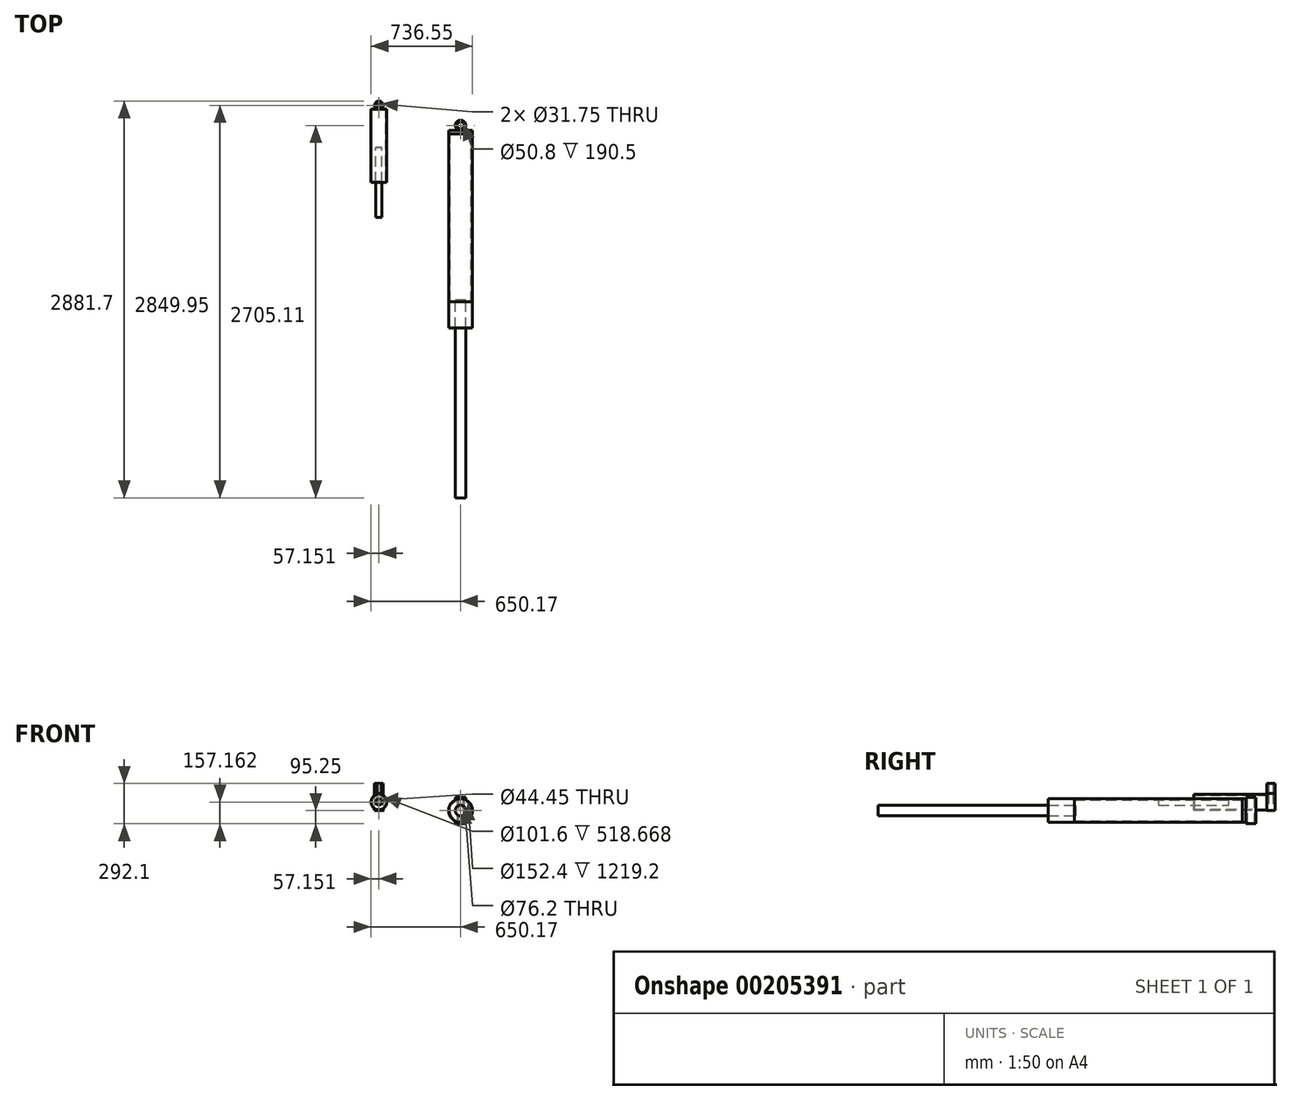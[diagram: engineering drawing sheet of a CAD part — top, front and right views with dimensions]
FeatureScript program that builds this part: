
annotation { "Feature Type Name" : "Feature", "Feature Type Description" : "" }
export const myFeature = defineFeature(function(context is Context, id is Id, definition is map)
    precondition{}
    {
        {
            var Q0;
            Q0=qCreatedBy(makeId("Front.planeOp"),FACE);
            var sketch = newSketch(context, id + "F0", { "sketchPlane" : qUnion([Q0])});
            skCircle(sketch, "E0", {"center": v(0, 0) * mm, "radius": 85.73 * mm});
            skCircle(sketch, "E1.0", {"center": v(0, 0) * mm, "radius": 76.2 * mm});
            skSolve(sketch);
        }
        {
            var Q0;
            Q0=makeQuery(id+"F0.imprint","IMPRINT",FACE,{"disambiguationData":[TD([[makeQuery(id+"F0.imprint","IMPRINT",EDGE,{"derivedFrom":sQuery(id+"F0.wireOp",EDGE,"E0")}),1.0]])]});
            extrude(context, id + "F1", {"entities" : qUnion([Q0]), "depth" : 1219.2 * mm});
        }
        {
            var Q0;
            Q0=makeQuery(id+"F1.opExtrude","CAP_FACE",FACE,{"disambiguationData":[OSD([sQuery(id+"F0.wireOp",EDGE,"E0"),sQuery(id+"F0.wireOp",EDGE,"E1.0")])],"isStart":false});
            var sketch = newSketch(context, id + "F2", { "sketchPlane" : qUnion([Q0])});
            skCircle(sketch, "E2", {"center": v(0, 0) * mm, "radius": 85.59 * mm});
            skCircle(sketch, "E3", {"center": v(0, 0) * mm, "radius": 38.1 * mm});
            skSolve(sketch);
        }
        {
            var Q0;
            Q0=makeQuery(id+"F2.imprint","IMPRINT",FACE,{"disambiguationData":[TD([[makeQuery(id+"F2.imprint","IMPRINT",EDGE,{"derivedFrom":sQuery(id+"F2.wireOp",EDGE,"E2")}),1.0]])]});
            var Q1;
            Q1=makeQuery(id+"F2.imprint","IMPRINT",FACE,{"disambiguationData":[TD([[makeQuery(id+"F2.imprint","IMPRINT",EDGE,{"derivedFrom":sQuery(id+"F2.wireOp",EDGE,"E3")}),-1.0]])]});
            extrude(context, id + "F3", {"entities" : qUnion([Q0, Q1]), "operationType" : NewBodyOperationType.ADD, "depth" : 190.5 * mm});
        }
        {
            var Q0;
            Q0=makeQuery(id+"F1.opExtrude","CAP_FACE",FACE,{"disambiguationData":[OSD([sQuery(id+"F0.wireOp",EDGE,"E0"),sQuery(id+"F0.wireOp",EDGE,"E1.0")])],"isStart":true});
            var sketch = newSketch(context, id + "F4", { "sketchPlane" : qUnion([Q0])});
            skCircle(sketch, "E4", {"center": v(0, 0) * mm, "radius": 86.38 * mm});
            skSolve(sketch);
        }
        {
            var Q0;
            Q0=makeQuery(id+"F4.imprint","IMPRINT",FACE,{"disambiguationData":[TD([[makeQuery(id+"F4.imprint","IMPRINT",EDGE,{"derivedFrom":sQuery(id+"F4.wireOp",EDGE,"E4")}),1.0]])]});
            var Q1;
            Q1=makeQuery(id+"F4.imprint","IMPRINT",FACE,{"disambiguationData":[TD([[makeQuery(id+"F4.imprint","IMPRINT",EDGE,{"derivedFrom":makeQuery(id+"F1.opExtrude","CAP_EDGE",EDGE,{"disambiguationData":[OSD([sQuery(id+"F0.wireOp",EDGE,"E0")])],"isStart":true})}),-1.0]])]});
            var Q2;
            Q2=makeQuery(id+"F4.imprint","IMPRINT",FACE,{"disambiguationData":[TD([[makeQuery(id+"F4.imprint","IMPRINT",EDGE,{"derivedFrom":makeQuery(id+"F1.opExtrude","CAP_EDGE",EDGE,{"disambiguationData":[OSD([sQuery(id+"F0.wireOp",EDGE,"E1.0")])],"isStart":true})}),-1.0]])]});
            extrude(context, id + "F5", {"entities" : qUnion([Q0, Q1, Q2]), "operationType" : NewBodyOperationType.ADD, "depth" : 25.4 * mm});
        }
        {
            var Q0;
            Q0=qCreatedBy(makeId("Top.planeOp"),FACE);
            var sketch = newSketch(context, id + "F6", { "sketchPlane" : qUnion([Q0])});
            skArc(sketch, "E5", {"start": v(15.23, 25.4) * mm, "mid": v(0, 98.42) * mm, "end": v(-15.23, 25.4) * mm});
            skCircle(sketch, "E6.0", {"center": v(0, 60.33) * mm, "radius": 25.4 * mm});
            skLineSegment(sketch, "E7", {"start": v(15.23, 25.4) * mm, "end": v(-15.23, 25.4) * mm});
            skSolve(sketch);
        }
        {
            var Q0;
            Q0=makeQuery(id+"F6.imprint","IMPRINT",FACE,{"disambiguationData":[TD([[makeQuery(id+"F6.imprint","IMPRINT",EDGE,{"derivedFrom":sQuery(id+"F6.wireOp",EDGE,"E5")}),1.0]])]});
            extrude(context, id + "F7", {"entities" : qUnion([Q0]), "depth" : 190.5 * mm, "symmetric" : true});
        }
        {
            var Q0;
            Q0=makeQuery(id+"F3.opExtrude","CAP_FACE",FACE,{"disambiguationData":[OSD([sQuery(id+"F2.wireOp",EDGE,"E2"),sQuery(id+"F2.wireOp",EDGE,"E3")])],"isStart":false});
            var sketch = newSketch(context, id + "F8", { "sketchPlane" : qUnion([Q0])});
            skCircle(sketch, "E8", {"center": v(0, 0) * mm, "radius": 38.1 * mm});
            skSolve(sketch);
        }
        {
            var Q0;
            Q0 = qSketchRegion(id + "F8", true);
            extrude(context, id + "F9", {"entities" : qUnion([Q0]), "depth" : 1235.07 * mm, "hasSecondDirection" : true, "secondDirectionOppositeDirection" : true, "secondDirectionDepth" : 203.2 * mm});
        }
        {
            var Q0;
            Q0=makeQuery(id+"F1.opExtrude","SWEPT_BODY",BODY,{"disambiguationData":[OSD([sQuery(id+"F0.wireOp",EDGE,"E0"),sQuery(id+"F0.wireOp",EDGE,"E1.0")])]});
            transform(context, id + "F10", {"entities" : qUnion([Q0]), "transformType" : TransformType.TRANSLATION_3D, "dx" : -444.5 * mm, "dy" : 0 * mm, "dz" : 0 * mm, "makeCopy" : true});
        }
        {
            var Q0;
            Q0=makeQuery(id+"F7.opExtrude","SWEPT_BODY",BODY,{"disambiguationData":[OSD([sQuery(id+"F6.wireOp",EDGE,"E5"),sQuery(id+"F6.wireOp",EDGE,"E6.0"),sQuery(id+"F6.wireOp",EDGE,"E7")])]});
            transform(context, id + "F11", {"entities" : qUnion([Q0]), "transformType" : TransformType.TRANSLATION_3D, "dx" : -347.98 * mm, "dy" : 0 * mm, "dz" : 0 * mm, "makeCopy" : true});
        }
        {
            var Q0;
            Q0=makeQuery(id+"F9.opExtrude","SWEPT_BODY",BODY,{"disambiguationData":[OSD([sQuery(id+"F8.wireOp",EDGE,"E8")])]});
            transform(context, id + "F12", {"entities" : qUnion([Q0]), "transformType" : TransformType.TRANSLATION_3D, "dx" : -424.18 * mm, "dy" : 0 * mm, "dz" : 0 * mm, "makeCopy" : true});
        }
        {
            var Q0;
            Q0=makeQuery(id+"F12.opPattern","COPY",BODY,{"derivedFrom":makeQuery(id+"F9.opExtrude","SWEPT_BODY",BODY,{"disambiguationData":[OSD([sQuery(id+"F8.wireOp",EDGE,"E8")])]}),"instanceName":"1"});
            deleteBodies(context, id + "F13", {"entities" : qUnion([Q0])});
        }
        {
            var Q0;
            Q0=makeQuery(id+"F10.opPattern","COPY",BODY,{"derivedFrom":makeQuery(id+"F1.opExtrude","SWEPT_BODY",BODY,{"disambiguationData":[OSD([sQuery(id+"F0.wireOp",EDGE,"E0"),sQuery(id+"F0.wireOp",EDGE,"E1.0")])]}),"instanceName":"1"});
            deleteBodies(context, id + "F14", {"entities" : qUnion([Q0])});
        }
        {
            var Q0;
            Q0=makeQuery(id+"F11.opPattern","COPY",BODY,{"derivedFrom":makeQuery(id+"F7.opExtrude","SWEPT_BODY",BODY,{"disambiguationData":[OSD([sQuery(id+"F6.wireOp",EDGE,"E5"),sQuery(id+"F6.wireOp",EDGE,"E6.0"),sQuery(id+"F6.wireOp",EDGE,"E7")])]}),"instanceName":"1"});
            deleteBodies(context, id + "F15", {"entities" : qUnion([Q0])});
        }
        {
            var Q0;
            Q0=qCreatedBy(makeId("Top.planeOp"),FACE);
            var sketch = newSketch(context, id + "F16", { "sketchPlane" : qUnion([Q0])});
            skArc(sketch, "E9", {"start": v(-575.8, 178.5) * mm, "mid": v(-593.02, 236.92) * mm, "end": v(-610.25, 178.5) * mm});
            skCircle(sketch, "E10.0", {"center": v(-593.02, 205.17) * mm, "radius": 15.88 * mm});
            skLineSegment(sketch, "E11", {"start": v(-610.25, 178.5) * mm, "end": v(-575.8, 178.5) * mm});
            skSolve(sketch);
        }
        {
            var Q0;
            Q0=makeQuery(id+"F16.imprint","IMPRINT",FACE,{"disambiguationData":[TD([[makeQuery(id+"F16.imprint","IMPRINT",EDGE,{"derivedFrom":sQuery(id+"F16.wireOp",EDGE,"E9")}),1.0]])]});
            extrude(context, id + "F17", {"entities" : qUnion([Q0]), "depth" : 123.82 * mm});
        }
        {
            var Q0;
            Q0=makeQuery(id+"F17.opExtrude","CAP_FACE",FACE,{"disambiguationData":[OSD([sQuery(id+"F16.wireOp",EDGE,"E9"),sQuery(id+"F16.wireOp",EDGE,"E10.0")])],"isStart":false});
            extrude(context, id + "F18", {"entities" : qUnion([Q0]), "depth" : 73.02 * mm});
        }
        {
            var Q0;
            Q0=makeQuery(id+"F17.opExtrude","SWEPT_FACE",FACE,{"disambiguationData":[OSD([sQuery(id+"F16.wireOp",EDGE,"E11")])]});
            var sketch = newSketch(context, id + "F19", { "sketchPlane" : qUnion([Q0])});
            skCircle(sketch, "E12", {"center": v(-593.02, 61.91) * mm, "radius": 57.15 * mm});
            skPoint(sketch, "E12.centerSnap0", {"position": v(-593.02, 0) * mm});
            skPoint(sketch, "E12.centerSnap1", {"position": v(-610.25, 61.91) * mm});
            skCircle(sketch, "E13.0", {"center": v(-593.02, 61.91) * mm, "radius": 50.8 * mm});
            skSolve(sketch);
        }
        {
            var Q0;
            {var subQ0=sQuery(id+"F19.wireOp",EDGE,"E12");var subQ1=sQuery(id+"F16.wireOp",EDGE,"E11");var subQ2=sQuery(id+"F16.wireOp",EDGE,"E9");var subQ3=makeQuery(id+"F17.opExtrude","SWEPT_EDGE",EDGE,{"disambiguationData":[OSD([subQ2,subQ1]),TDD([makeQuery(id+"F16.imprint","INTERSECT",VERTEX,{"disambiguationData":[OD(1.0)],"derivedFrom":[subQ2,subQ1]})])]});var subQ4=makeQuery(id+"F19.imprint","INTERSECT",VERTEX,{"disambiguationData":[OD(0.0)],"derivedFrom":[subQ3,subQ0]});Q0=makeQuery(id+"F19.imprint","IMPRINT",FACE,{"disambiguationData":[TD([[makeQuery(id+"F19.imprint","IMPRINT",EDGE,{"disambiguationData":[TD([[subQ4,-1.0]])],"derivedFrom":subQ0}),1.0]])]});}
            var Q1;
            {var subQ0=sQuery(id+"F19.wireOp",EDGE,"E12");var subQ1=sQuery(id+"F16.wireOp",EDGE,"E11");var subQ2=sQuery(id+"F16.wireOp",EDGE,"E9");var subQ3=makeQuery(id+"F17.opExtrude","SWEPT_EDGE",EDGE,{"disambiguationData":[OSD([subQ2,subQ1]),TDD([makeQuery(id+"F16.imprint","INTERSECT",VERTEX,{"disambiguationData":[OD(1.0)],"derivedFrom":[subQ2,subQ1]})])]});var subQ4=makeQuery(id+"F19.imprint","INTERSECT",VERTEX,{"disambiguationData":[OD(1.0)],"derivedFrom":[subQ3,subQ0]});Q1=makeQuery(id+"F19.imprint","IMPRINT",FACE,{"disambiguationData":[TD([[makeQuery(id+"F19.imprint","IMPRINT",EDGE,{"disambiguationData":[TD([[subQ4,-1.0]])],"derivedFrom":subQ0}),1.0]])]});}
            var Q2;
            {var subQ0=sQuery(id+"F19.wireOp",EDGE,"E12");var subQ1=sQuery(id+"F16.wireOp",EDGE,"E11");var subQ2=sQuery(id+"F16.wireOp",EDGE,"E9");var subQ3=makeQuery(id+"F17.opExtrude","SWEPT_EDGE",EDGE,{"disambiguationData":[OSD([subQ2,subQ1]),TDD([makeQuery(id+"F16.imprint","INTERSECT",VERTEX,{"disambiguationData":[OD(1.0)],"derivedFrom":[subQ2,subQ1]})])]});var subQ4=makeQuery(id+"F19.imprint","INTERSECT",VERTEX,{"disambiguationData":[OD(0.0)],"derivedFrom":[subQ3,subQ0]});Q2=makeQuery(id+"F19.imprint","IMPRINT",FACE,{"disambiguationData":[TD([[makeQuery(id+"F19.imprint","IMPRINT",EDGE,{"disambiguationData":[TD([[subQ4,1.0]])],"derivedFrom":subQ0}),1.0]])]});}
            var Q3;
            {var subQ0=sQuery(id+"F19.wireOp",EDGE,"E12");var subQ1=sQuery(id+"F16.wireOp",EDGE,"E11");var subQ2=sQuery(id+"F16.wireOp",EDGE,"E9");var subQ3=makeQuery(id+"F17.opExtrude","SWEPT_EDGE",EDGE,{"disambiguationData":[OSD([subQ2,subQ1]),TDD([makeQuery(id+"F16.imprint","INTERSECT",VERTEX,{"disambiguationData":[OD(0.0)],"derivedFrom":[subQ2,subQ1]})])]});var subQ4=makeQuery(id+"F19.imprint","INTERSECT",VERTEX,{"disambiguationData":[OD(0.0)],"derivedFrom":[subQ3,subQ0]});Q3=makeQuery(id+"F19.imprint","IMPRINT",FACE,{"disambiguationData":[TD([[makeQuery(id+"F19.imprint","IMPRINT",EDGE,{"disambiguationData":[TD([[subQ4,1.0]])],"derivedFrom":subQ0}),1.0]])]});}
            extrude(context, id + "F20", {"entities" : qUnion([Q0, Q1, Q2, Q3]), "depth" : 531.37 * mm});
        }
        {
            var Q0;
            Q0=makeQuery(id+"F20.opExtrude","CAP_FACE",FACE,{"disambiguationData":[OSD([sQuery(id+"F19.wireOp",EDGE,"E12"),sQuery(id+"F19.wireOp",EDGE,"E13.0")])],"isStart":true});
            var sketch = newSketch(context, id + "F21", { "sketchPlane" : qUnion([Q0])});
            skCircle(sketch, "E14", {"center": v(593.02, 61.91) * mm, "radius": 57.15 * mm});
            skSolve(sketch);
        }
        {
            var Q0;
            Q0 = qSketchRegion(id + "F21", true);
            extrude(context, id + "F22", {"entities" : qUnion([Q0]), "operationType" : NewBodyOperationType.ADD, "oppositeDirection" : true, "depth" : 6.35 * mm});
        }
        {
            var Q0;
            Q0=makeQuery(id+"F20.opExtrude","CAP_FACE",FACE,{"disambiguationData":[OSD([sQuery(id+"F19.wireOp",EDGE,"E12"),sQuery(id+"F19.wireOp",EDGE,"E13.0")])],"isStart":false});
            var sketch = newSketch(context, id + "F23", { "sketchPlane" : qUnion([Q0])});
            skCircle(sketch, "E15", {"center": v(-593.02, 61.91) * mm, "radius": 56.77 * mm});
            skSolve(sketch);
        }
        {
            var Q0;
            Q0 = qSketchRegion(id + "F23", true);
            extrude(context, id + "F24", {"entities" : qUnion([Q0]), "operationType" : NewBodyOperationType.ADD, "oppositeDirection" : true, "depth" : 6.35 * mm});
        }
        {
            var Q0;
            Q0=makeQuery(id+"F24.boolean.opBoolean","MERGE",FACE,{"derivedFrom":[makeQuery(id+"F20.opExtrude","CAP_FACE",FACE,{"disambiguationData":[OSD([sQuery(id+"F19.wireOp",EDGE,"E12"),sQuery(id+"F19.wireOp",EDGE,"E13.0")])],"isStart":false}),makeQuery(id+"F24.opExtrude","CAP_FACE",FACE,{"disambiguationData":[OSD([sQuery(id+"F23.wireOp",EDGE,"E15")])],"isStart":true})]});
            var sketch = newSketch(context, id + "F25", { "sketchPlane" : qUnion([Q0])});
            skCircle(sketch, "E16", {"center": v(-593.02, 61.91) * mm, "radius": 22.23 * mm});
            skSolve(sketch);
        }
        {
            var Q0;
            Q0=makeQuery(id+"F25.imprint","IMPRINT",FACE,{"disambiguationData":[TD([[makeQuery(id+"F25.imprint","IMPRINT",EDGE,{"derivedFrom":sQuery(id+"F25.wireOp",EDGE,"E16")}),1.0]])]});
            extrude(context, id + "F26", {"entities" : qUnion([Q0]), "depth" : 508 * mm, "symmetric" : true});
        }
        {
            var Q0;
            Q0=makeQuery(id+"F26.opExtrude","SWEPT_BODY",BODY,{"disambiguationData":[OSD([sQuery(id+"F25.wireOp",EDGE,"E16")])]});
            var Q1;
            Q1=makeQuery(id+"F17.opExtrude","SWEPT_BODY",BODY,{"disambiguationData":[OSD([sQuery(id+"F16.wireOp",EDGE,"E9"),sQuery(id+"F16.wireOp",EDGE,"E10.0"),sQuery(id+"F16.wireOp",EDGE,"E11")])]});
            booleanBodies(context, id + "F27", {"operationType" : BooleanOperationType.SUBTRACTION, "tools" : qUnion([Q0]), "targets" : qUnion([Q1]), "keepTools" : true});
        }
    });
